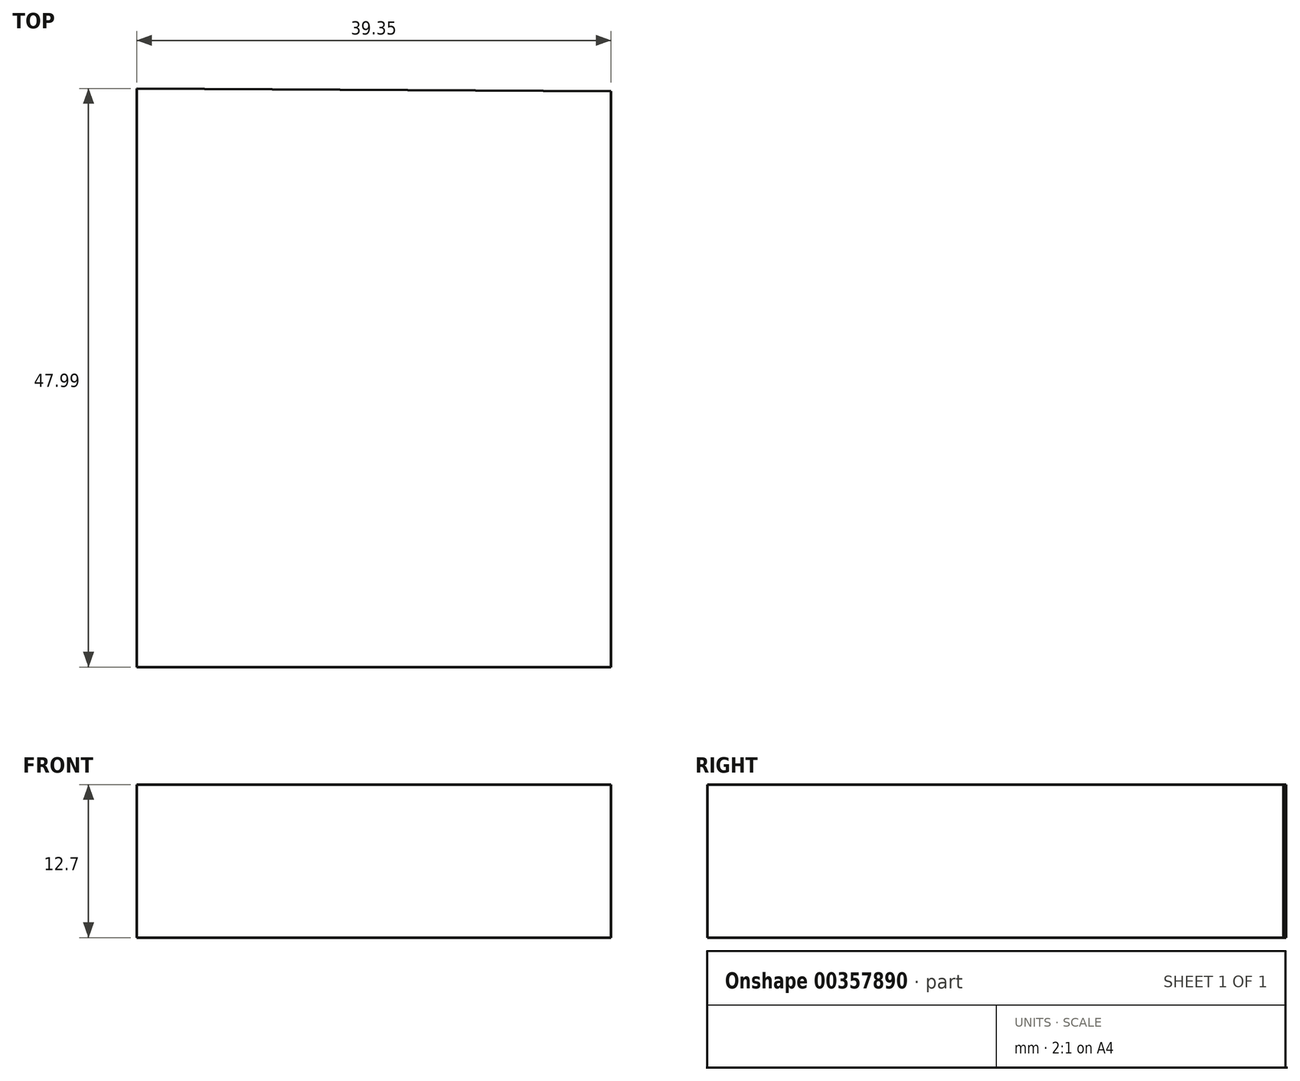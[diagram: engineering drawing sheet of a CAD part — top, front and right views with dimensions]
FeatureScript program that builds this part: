
annotation { "Feature Type Name" : "Feature", "Feature Type Description" : "" }
export const myFeature = defineFeature(function(context is Context, id is Id, definition is map)
    precondition{}
    {
        {
            var Q0;
            Q0=qCreatedBy(makeId("Top.planeOp"),FACE);
            var sketch = newSketch(context, id + "F0", { "sketchPlane" : qUnion([Q0])});
            skLineSegment(sketch, "E0", {"start": v(-39.35, -10.54) * mm, "end": v(-39.35, 37.45) * mm});
            skLineSegment(sketch, "E1", {"start": v(0, -7.93) * mm, "end": v(0, 37.24) * mm});
            skLineSegment(sketch, "E2", {"start": v(0, 37.24) * mm, "end": v(-39.35, 37.45) * mm});
            skLineSegment(sketch, "E3", {"start": v(-39.35, -10.54) * mm, "end": v(0, -10.54) * mm});
            skLineSegment(sketch, "E4", {"start": v(0, -10.54) * mm, "end": v(0, -7.93) * mm});
            skSolve(sketch);
        }
        {
            var Q0;
            Q0=makeQuery(id+"F0.imprint","IMPRINT",FACE,{"disambiguationData":[TD([[makeQuery(id+"F0.imprint","IMPRINT",EDGE,{"derivedFrom":sQuery(id+"F0.wireOp",EDGE,"E0")}),-1.0]])]});
            extrude(context, id + "F1", {"entities" : qUnion([Q0]), "depth" : 12.7 * mm});
        }
    });
